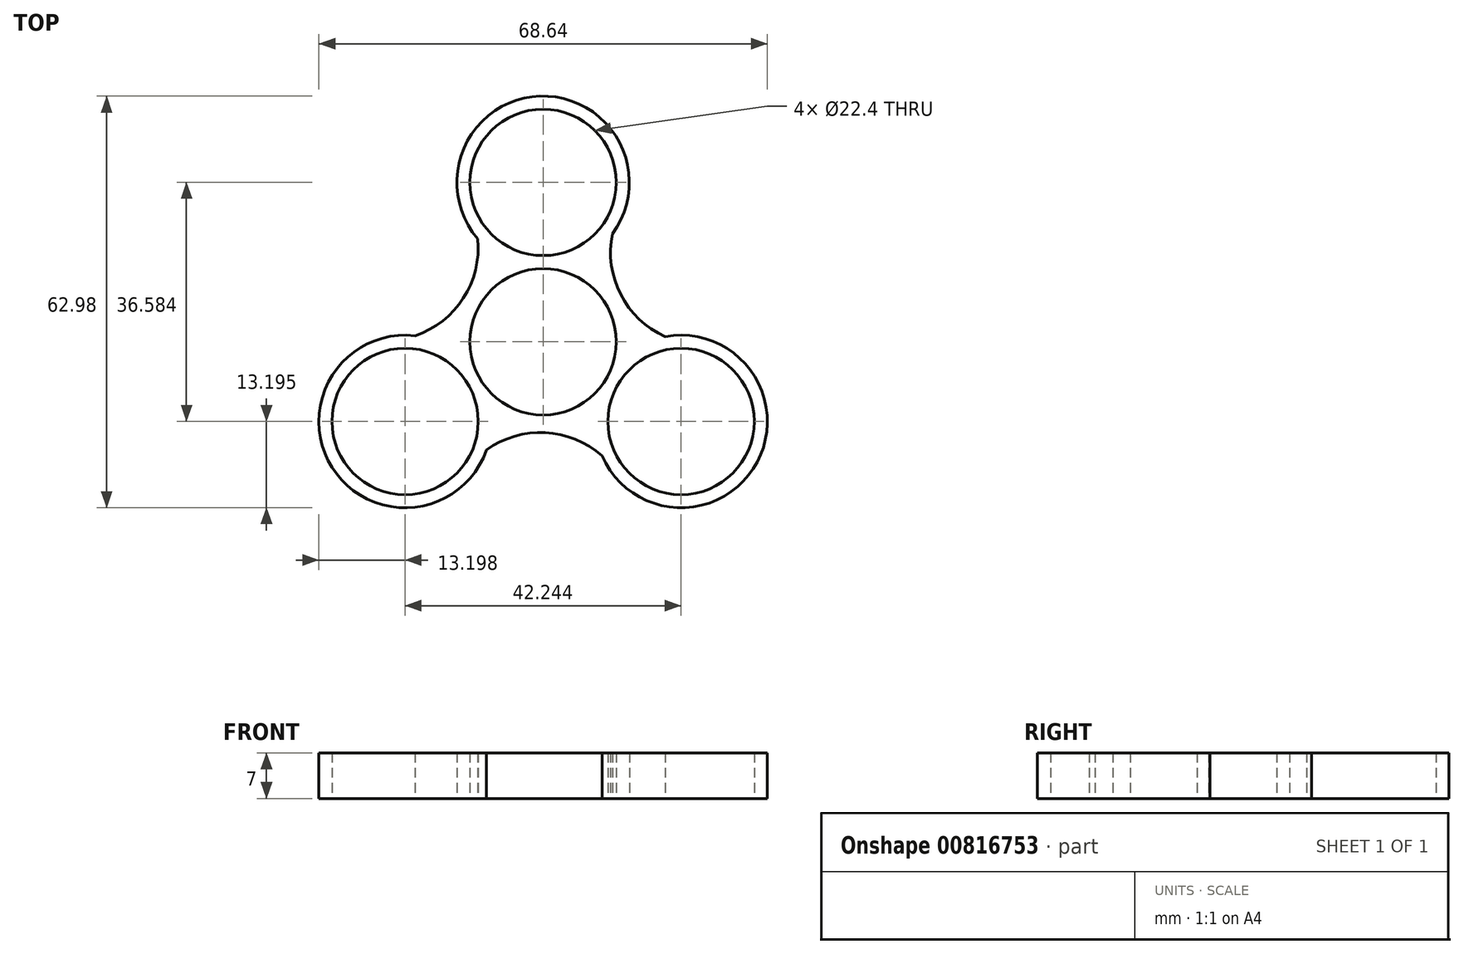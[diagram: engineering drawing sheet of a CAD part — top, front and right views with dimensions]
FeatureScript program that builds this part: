
annotation { "Feature Type Name" : "Feature", "Feature Type Description" : "" }
export const myFeature = defineFeature(function(context is Context, id is Id, definition is map)
    precondition{}
    {
        {
            var Q0;
            Q0=qCreatedBy(makeId("Top.planeOp"),FACE);
            var sketch = newSketch(context, id + "F0", { "sketchPlane" : qUnion([Q0])});
            skCircle(sketch, "E0", {"center": v(0, 0) * mm, "radius": 11.2 * mm});
            skCircle(sketch, "E1", {"center": v(0, 24.39) * mm, "radius": 13.2 * mm});
            skCircle(sketch, "E2", {"center": v(0, 24.39) * mm, "radius": 11.2 * mm});
            skCircle(sketch, "E3.1.0", {"center": v(-21.12, -12.2) * mm, "radius": 11.2 * mm});
            skCircle(sketch, "E3.1.1", {"center": v(-21.12, -12.2) * mm, "radius": 13.2 * mm});
            skCircle(sketch, "E3.2.0", {"center": v(21.12, -12.2) * mm, "radius": 11.2 * mm});
            skCircle(sketch, "E3.2.1", {"center": v(21.12, -12.2) * mm, "radius": 13.2 * mm});
            skArc(sketch, "E4", {"start": v(-19.62, 0.92) * mm, "mid": v(-12.2, 6.67) * mm, "end": v(-10.02, 15.8) * mm});
            skArc(sketch, "E5.1.0", {"start": v(9.01, -17.45) * mm, "mid": v(0.33, -13.9) * mm, "end": v(-8.67, -16.57) * mm});
            skArc(sketch, "E5.2.0", {"start": v(10.6, 16.53) * mm, "mid": v(11.88, 7.24) * mm, "end": v(18.69, 0.78) * mm});
            skSolve(sketch);
        }
        {
            var Q0;
            Q0=makeQuery(id+"F0.imprint","IMPRINT",FACE,{"disambiguationData":[TD([[makeQuery(id+"F0.imprint","IMPRINT",EDGE,{"derivedFrom":sQuery(id+"F0.wireOp",EDGE,"E2")}),-1.0]])]});
            var Q1;
            Q1=makeQuery(id+"F0.imprint","IMPRINT",FACE,{"disambiguationData":[TD([[makeQuery(id+"F0.imprint","IMPRINT",EDGE,{"derivedFrom":sQuery(id+"F0.wireOp",EDGE,"E3.2.0")}),-1.0]])]});
            var Q2;
            Q2=makeQuery(id+"F0.imprint","IMPRINT",FACE,{"disambiguationData":[TD([[makeQuery(id+"F0.imprint","IMPRINT",EDGE,{"derivedFrom":sQuery(id+"F0.wireOp",EDGE,"E3.1.0")}),-1.0]])]});
            var Q3;
            {var subQ5=sQuery(id+"F0.wireOp",EDGE,"E4");Q3=makeQuery(id+"F0.imprint","IMPRINT",FACE,{"disambiguationData":[TD([[makeQuery(id+"F0.imprint","IMPRINT",EDGE,{"derivedFrom":subQ5}),-1.0]])]});}
            var Q4;
            {var subQ5=sQuery(id+"F0.wireOp",EDGE,"E5.2.0");Q4=makeQuery(id+"F0.imprint","IMPRINT",FACE,{"disambiguationData":[TD([[makeQuery(id+"F0.imprint","IMPRINT",EDGE,{"derivedFrom":subQ5}),-1.0]])]});}
            var Q5;
            {var subQ5=sQuery(id+"F0.wireOp",EDGE,"E5.1.0");Q5=makeQuery(id+"F0.imprint","IMPRINT",FACE,{"disambiguationData":[TD([[makeQuery(id+"F0.imprint","IMPRINT",EDGE,{"derivedFrom":subQ5}),-1.0]])]});}
            extrude(context, id + "F1", {"entities" : qUnion([Q0, Q1, Q2, Q3, Q4, Q5]), "depth" : 7 * mm, "offsetDistance" : 25 * mm});
        }
    });
